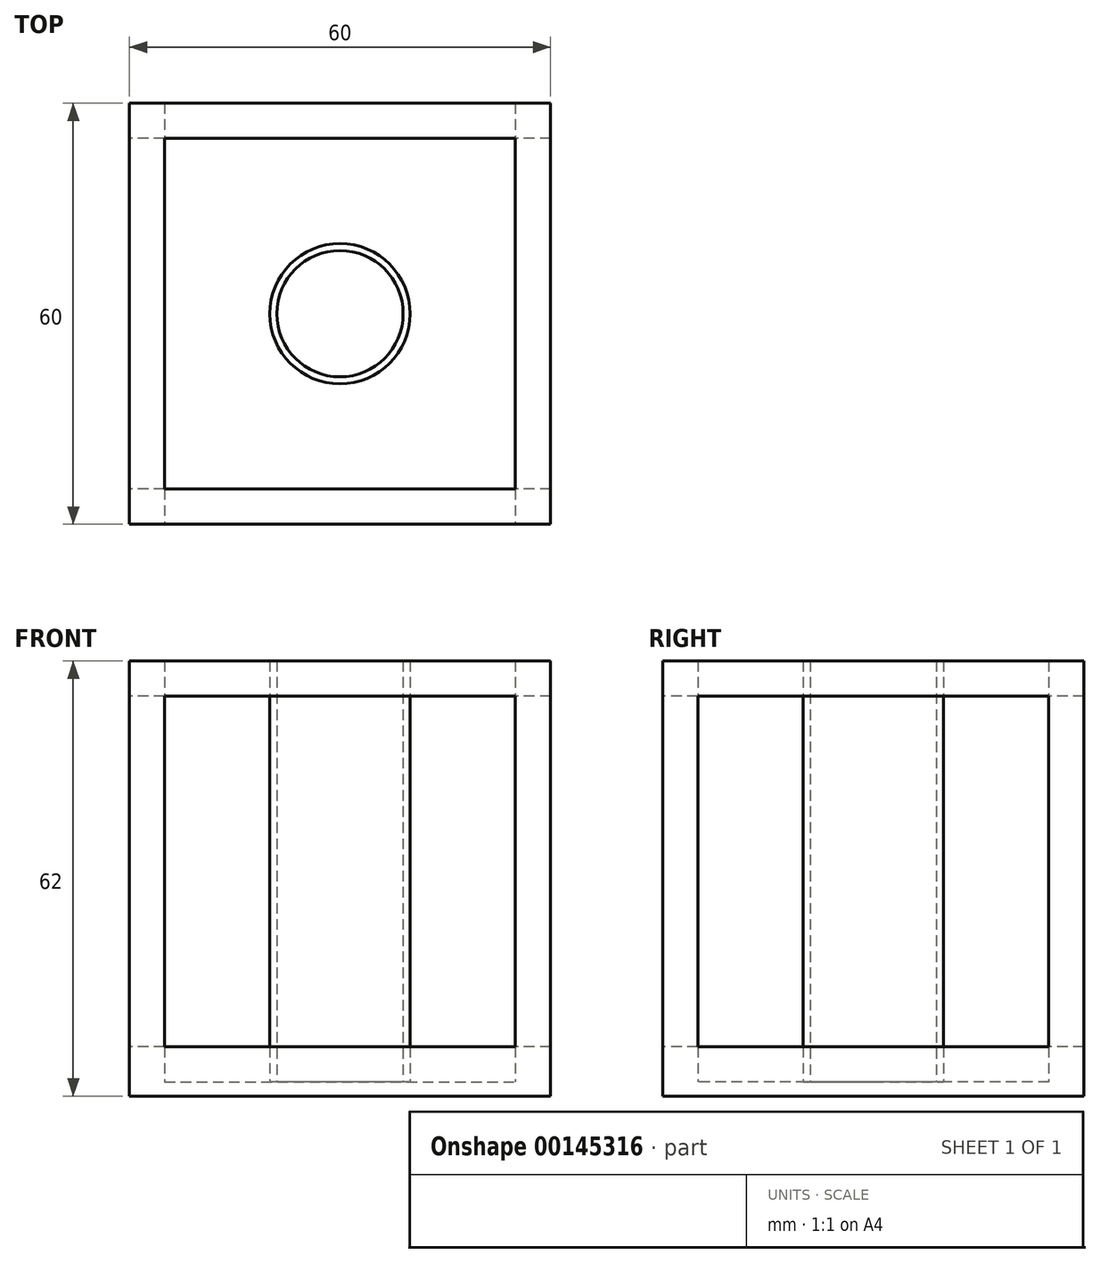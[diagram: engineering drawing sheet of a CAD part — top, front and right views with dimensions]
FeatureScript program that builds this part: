
annotation { "Feature Type Name" : "Feature", "Feature Type Description" : "" }
export const myFeature = defineFeature(function(context is Context, id is Id, definition is map)
    precondition{}
    {
        {
            var Q0;
            Q0=qCreatedBy(makeId("Top.planeOp"),FACE);
            var sketch = newSketch(context, id + "F0", { "sketchPlane" : qUnion([Q0])});
            skLineSegment(sketch, "E0.bottom", {"start": v(-30, 30) * mm, "end": v(30, 30) * mm});
            skLineSegment(sketch, "E0.top", {"start": v(-30, -30) * mm, "end": v(30, -30) * mm});
            skLineSegment(sketch, "E0.left", {"start": v(-30, 30) * mm, "end": v(-30, -30) * mm});
            skLineSegment(sketch, "E0.right", {"start": v(30, 30) * mm, "end": v(30, -30) * mm});
            skPoint(sketch, "E0.middle", {"position": v(0, 0) * mm});
            skLineSegment(sketch, "E1.bottom", {"start": v(-25, 25) * mm, "end": v(25, 25) * mm});
            skLineSegment(sketch, "E1.top", {"start": v(-25, -25) * mm, "end": v(25, -25) * mm});
            skLineSegment(sketch, "E1.left", {"start": v(-25, 25) * mm, "end": v(-25, -25) * mm});
            skLineSegment(sketch, "E1.right", {"start": v(25, 25) * mm, "end": v(25, -25) * mm});
            skCircle(sketch, "E2", {"center": v(0, 0) * mm, "radius": 10 * mm});
            skCircle(sketch, "E3", {"center": v(0, 0) * mm, "radius": 9 * mm});
            skSolve(sketch);
        }
        {
            var Q0;
            Q0 = qSketchRegion(id + "F0", true);
            var Q1;
            Q1=makeQuery(id+"F0.imprint","IMPRINT",FACE,{"disambiguationData":[TD([[makeQuery(id+"F0.imprint","IMPRINT",EDGE,{"derivedFrom":sQuery(id+"F0.wireOp",EDGE,"E1.bottom")}),-1.0]])]});
            var Q2;
            Q2=makeQuery(id+"F0.imprint","IMPRINT",FACE,{"disambiguationData":[TD([[makeQuery(id+"F0.imprint","IMPRINT",EDGE,{"derivedFrom":sQuery(id+"F0.wireOp",EDGE,"E3")}),1.0]])]});
            var Q3;
            Q3=makeQuery(id+"F0.imprint","IMPRINT",FACE,{"disambiguationData":[TD([[makeQuery(id+"F0.imprint","IMPRINT",EDGE,{"derivedFrom":sQuery(id+"F0.wireOp",EDGE,"E2")}),1.0]])]});
            extrude(context, id + "F1", {"entities" : qUnion([Q0, Q1, Q2, Q3]), "oppositeDirection" : true, "depth" : 2 * mm});
        }
        {
            var Q0;
            Q0=makeQuery(id+"F0.imprint","IMPRINT",FACE,{"disambiguationData":[TD([[makeQuery(id+"F0.imprint","IMPRINT",EDGE,{"derivedFrom":sQuery(id+"F0.wireOp",EDGE,"E0.bottom")}),-1.0]])]});
            extrude(context, id + "F2", {"entities" : qUnion([Q0]), "operationType" : NewBodyOperationType.ADD, "depth" : 60 * mm});
        }
        {
            var Q0;
            {var subQ0=sQuery(id+"F0.wireOp",EDGE,"E0.left");Q0=makeQuery(id+"F2.boolean.opBoolean","MERGE",FACE,{"derivedFrom":[makeQuery(id+"F1.opExtrude","SWEPT_FACE",FACE,{"disambiguationData":[OSD([subQ0])]}),makeQuery(id+"F2.opExtrude","SWEPT_FACE",FACE,{"disambiguationData":[OSD([subQ0])]})]});}
            var sketch = newSketch(context, id + "F3", { "sketchPlane" : qUnion([Q0])});
            skLineSegment(sketch, "E4.bottom", {"start": v(-25, 55) * mm, "end": v(25, 55) * mm});
            skLineSegment(sketch, "E4.top", {"start": v(-25, 5) * mm, "end": v(25, 5) * mm});
            skLineSegment(sketch, "E4.left", {"start": v(-25, 55) * mm, "end": v(-25, 5) * mm});
            skLineSegment(sketch, "E4.right", {"start": v(25, 55) * mm, "end": v(25, 5) * mm});
            skSolve(sketch);
        }
        {
            var Q0;
            Q0=makeQuery(id+"F3.imprint","IMPRINT",FACE,{"disambiguationData":[TD([[makeQuery(id+"F3.imprint","IMPRINT",EDGE,{"derivedFrom":sQuery(id+"F3.wireOp",EDGE,"E4.bottom")}),-1.0]])]});
            extrude(context, id + "F4", {"entities" : qUnion([Q0]), "operationType" : NewBodyOperationType.REMOVE, "endBound" : BoundingType.THROUGH_ALL, "oppositeDirection" : true, "depth" : 25 * mm});
        }
        {
            var Q0;
            {var subQ0=sQuery(id+"F0.wireOp",EDGE,"E0.top");Q0=makeQuery(id+"F2.boolean.opBoolean","MERGE",FACE,{"derivedFrom":[makeQuery(id+"F1.opExtrude","SWEPT_FACE",FACE,{"disambiguationData":[OSD([subQ0])]}),makeQuery(id+"F2.opExtrude","SWEPT_FACE",FACE,{"disambiguationData":[OSD([subQ0])]})]});}
            var sketch = newSketch(context, id + "F5", { "sketchPlane" : qUnion([Q0])});
            skLineSegment(sketch, "E5.bottom", {"start": v(-25, 55) * mm, "end": v(25, 55) * mm});
            skLineSegment(sketch, "E5.top", {"start": v(-25, 5) * mm, "end": v(25, 5) * mm});
            skLineSegment(sketch, "E5.left", {"start": v(-25, 55) * mm, "end": v(-25, 5) * mm});
            skLineSegment(sketch, "E5.right", {"start": v(25, 55) * mm, "end": v(25, 5) * mm});
            skSolve(sketch);
        }
        {
            var Q0;
            Q0=makeQuery(id+"F5.imprint","IMPRINT",FACE,{"disambiguationData":[TD([[makeQuery(id+"F5.imprint","IMPRINT",EDGE,{"derivedFrom":sQuery(id+"F5.wireOp",EDGE,"E5.bottom")}),-1.0]])]});
            extrude(context, id + "F6", {"entities" : qUnion([Q0]), "operationType" : NewBodyOperationType.REMOVE, "endBound" : BoundingType.THROUGH_ALL, "oppositeDirection" : true, "depth" : 25 * mm});
        }
        {
            var Q0;
            Q0=makeQuery(id+"F0.imprint","IMPRINT",FACE,{"disambiguationData":[TD([[makeQuery(id+"F0.imprint","IMPRINT",EDGE,{"derivedFrom":sQuery(id+"F0.wireOp",EDGE,"E2")}),1.0]])]});
            extrude(context, id + "F7", {"entities" : qUnion([Q0]), "operationType" : NewBodyOperationType.ADD, "depth" : 60 * mm});
        }
    });
